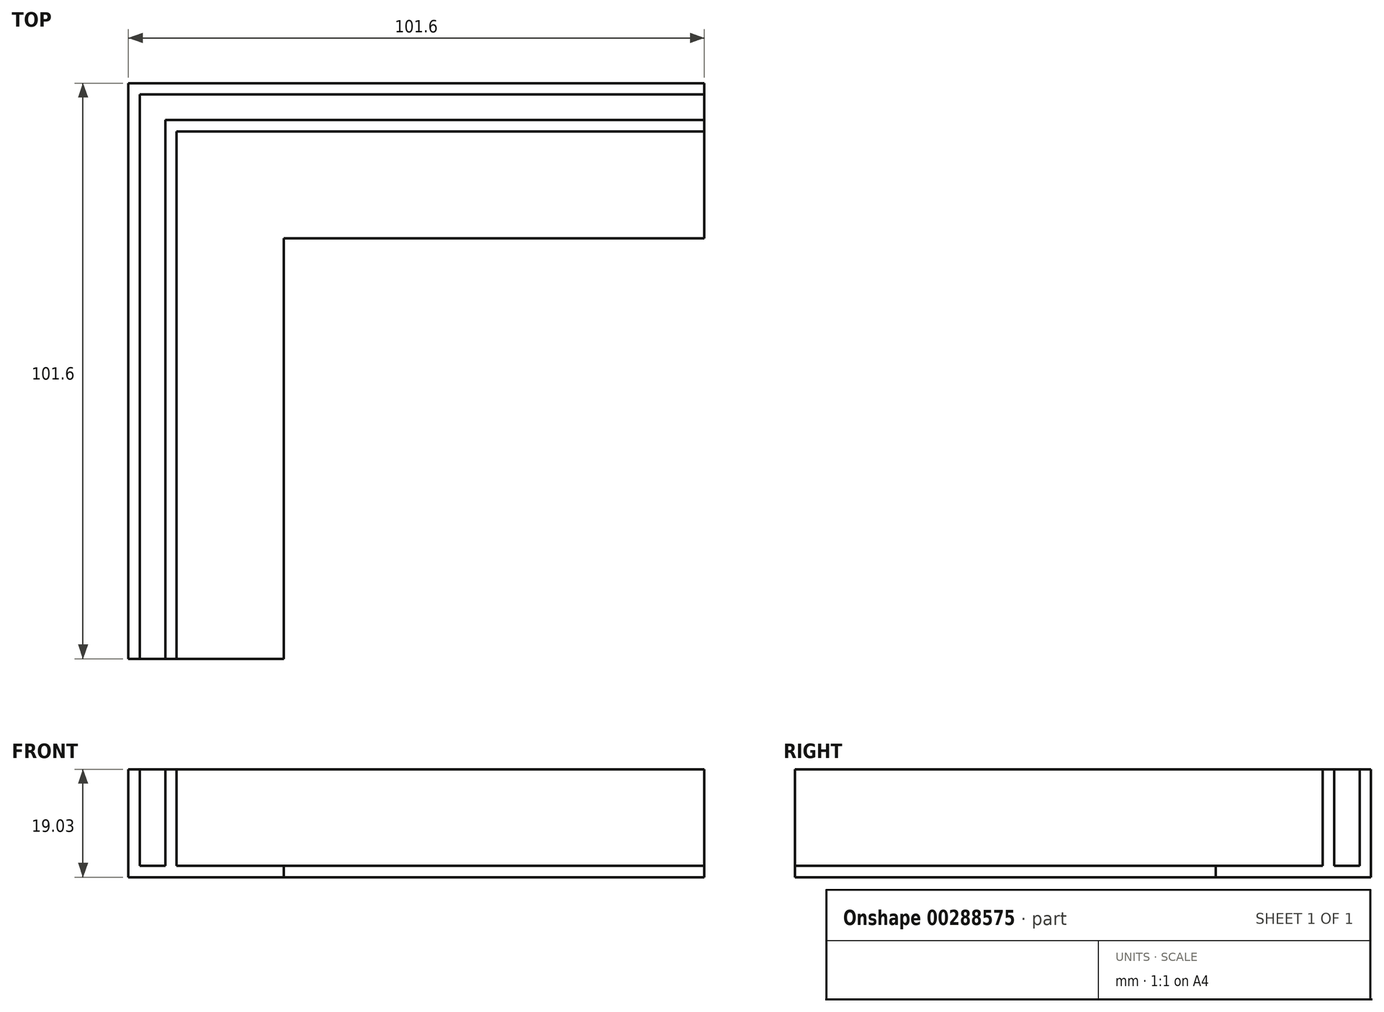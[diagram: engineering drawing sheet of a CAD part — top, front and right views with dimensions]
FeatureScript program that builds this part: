
annotation { "Feature Type Name" : "Feature", "Feature Type Description" : "" }
export const myFeature = defineFeature(function(context is Context, id is Id, definition is map)
    precondition{}
    {
        {
            var Q0;
            Q0=qCreatedBy(makeId("Top.planeOp"),FACE);
            var sketch = newSketch(context, id + "F0", { "sketchPlane" : qUnion([Q0])});
            skLineSegment(sketch, "E0.bottom", {"start": v(50.8, 50.8) * mm, "end": v(-50.8, 50.8) * mm});
            skLineSegment(sketch, "E0.top", {"start": v(50.8, -50.8) * mm, "end": v(-50.8, -50.8) * mm});
            skLineSegment(sketch, "E0.left", {"start": v(50.8, 50.8) * mm, "end": v(50.8, -50.8) * mm});
            skLineSegment(sketch, "E0.right", {"start": v(-50.8, 50.8) * mm, "end": v(-50.8, -50.8) * mm});
            skPoint(sketch, "E0.middle", {"position": v(0, 0) * mm});
            skSolve(sketch);
        }
        {
            var Q0;
            Q0 = qSketchRegion(id + "F0", true);
            extrude(context, id + "F1", {"entities" : qUnion([Q0]), "oppositeDirection" : true, "depth" : 2 * mm});
        }
        {
            var Q0;
            Q0=makeQuery(id+"F1.opExtrude","CAP_FACE",FACE,{"disambiguationData":[OSD([sQuery(id+"F0.wireOp",EDGE,"E0.bottom"),sQuery(id+"F0.wireOp",EDGE,"E0.top"),sQuery(id+"F0.wireOp",EDGE,"E0.left"),sQuery(id+"F0.wireOp",EDGE,"E0.right")])],"isStart":true});
            var sketch = newSketch(context, id + "F2", { "sketchPlane" : qUnion([Q0])});
            skLineSegment(sketch, "E1.right", {"start": v(-48.8, -50.8) * mm, "end": v(-48.8, 48.8) * mm});
            skLineSegment(sketch, "E2.top", {"start": v(50.8, 48.8) * mm, "end": v(-48.8, 48.8) * mm});
            skLineSegment(sketch, "E3", {"start": v(-50.8, 50.8) * mm, "end": v(-50.8, -50.8) * mm});
            skLineSegment(sketch, "E4", {"start": v(-50.8, -50.8) * mm, "end": v(-48.8, -50.8) * mm});
            skLineSegment(sketch, "E5", {"start": v(-50.8, 50.8) * mm, "end": v(50.8, 50.8) * mm});
            skLineSegment(sketch, "E6", {"start": v(50.8, 50.8) * mm, "end": v(50.8, 48.8) * mm});
            skSolve(sketch);
        }
        {
            var Q0;
            Q0=makeQuery(id+"F2.imprint","IMPRINT",FACE,{"disambiguationData":[TD([[makeQuery(id+"F2.imprint","IMPRINT",EDGE,{"derivedFrom":sQuery(id+"F2.wireOp",EDGE,"E1.right")}),1.0]])]});
            extrude(context, id + "F3", {"entities" : qUnion([Q0]), "operationType" : NewBodyOperationType.ADD, "depth" : 17.02 * mm});
        }
        {
            var Q0;
            Q0=makeQuery(id+"F1.opExtrude","CAP_FACE",FACE,{"disambiguationData":[OSD([sQuery(id+"F0.wireOp",EDGE,"E0.bottom"),sQuery(id+"F0.wireOp",EDGE,"E0.top"),sQuery(id+"F0.wireOp",EDGE,"E0.left"),sQuery(id+"F0.wireOp",EDGE,"E0.right")])],"isStart":true});
            var sketch = newSketch(context, id + "F4", { "sketchPlane" : qUnion([Q0])});
            skLineSegment(sketch, "E7.bottom", {"start": v(50.8, -50.8) * mm, "end": v(-44.3, -50.8) * mm});
            skLineSegment(sketch, "E7.top", {"start": v(50.8, 44.3) * mm, "end": v(-44.3, 44.3) * mm});
            skLineSegment(sketch, "E7.left", {"start": v(50.8, -50.8) * mm, "end": v(50.8, 44.3) * mm});
            skLineSegment(sketch, "E7.right", {"start": v(-44.3, -50.8) * mm, "end": v(-44.3, 44.3) * mm});
            skSolve(sketch);
        }
        {
            var Q0;
            Q0=makeQuery(id+"F4.imprint","IMPRINT",FACE,{"disambiguationData":[TD([[makeQuery(id+"F4.imprint","IMPRINT",EDGE,{"derivedFrom":sQuery(id+"F4.wireOp",EDGE,"E7.bottom")}),-1.0]])]});
            var Q1;
            Q1=makeQuery(id+"F3.opExtrude","CAP_FACE",FACE,{"disambiguationData":[OSD([sQuery(id+"F2.wireOp",EDGE,"E1.right"),sQuery(id+"F2.wireOp",EDGE,"E2.top"),sQuery(id+"F2.wireOp",EDGE,"E3"),sQuery(id+"F2.wireOp",EDGE,"E4"),sQuery(id+"F2.wireOp",EDGE,"E5"),sQuery(id+"F2.wireOp",EDGE,"E6")])],"isStart":false});
            extrude(context, id + "F5", {"entities" : qUnion([Q0]), "operationType" : NewBodyOperationType.ADD, "endBound" : BoundingType.UP_TO_SURFACE, "endBoundEntityFace" : qUnion([Q1]), "depth" : 25.4 * mm});
        }
        {
            var Q0;
            Q0=makeQuery(id+"F5.opExtrude","CAP_FACE",FACE,{"disambiguationData":[OSD([sQuery(id+"F4.wireOp",EDGE,"E7.bottom"),sQuery(id+"F4.wireOp",EDGE,"E7.top"),sQuery(id+"F4.wireOp",EDGE,"E7.left"),sQuery(id+"F4.wireOp",EDGE,"E7.right")])],"isStart":false});
            var sketch = newSketch(context, id + "F6", { "sketchPlane" : qUnion([Q0])});
            skLineSegment(sketch, "E8.bottom", {"start": v(50.8, -50.8) * mm, "end": v(-42.3, -50.8) * mm});
            skLineSegment(sketch, "E8.top", {"start": v(50.8, 42.3) * mm, "end": v(-42.3, 42.3) * mm});
            skLineSegment(sketch, "E8.left", {"start": v(50.8, -50.8) * mm, "end": v(50.8, 42.3) * mm});
            skLineSegment(sketch, "E8.right", {"start": v(-42.3, -50.8) * mm, "end": v(-42.3, 42.3) * mm});
            skSolve(sketch);
        }
        {
            var Q0;
            Q0=makeQuery(id+"F6.imprint","IMPRINT",FACE,{"disambiguationData":[TD([[makeQuery(id+"F6.imprint","IMPRINT",EDGE,{"derivedFrom":sQuery(id+"F6.wireOp",EDGE,"E8.bottom")}),-1.0]])]});
            extrude(context, id + "F7", {"entities" : qUnion([Q0]), "operationType" : NewBodyOperationType.REMOVE, "endBound" : BoundingType.THROUGH_ALL, "oppositeDirection" : true, "depth" : 59.5 * mm});
        }
        {
            var Q0;
            Q0=makeQuery(id+"F7.boolean.opBoolean","COPY",FACE,{"derivedFrom":makeQuery(id+"F7.opExtrude","SWEPT_FACE",FACE,{"disambiguationData":[OSD([sQuery(id+"F6.wireOp",EDGE,"E8.right")])]})});
            var sketch = newSketch(context, id + "F8", { "sketchPlane" : qUnion([Q0])});
            skLineSegment(sketch, "E9.bottom", {"start": v(-50.8, -2) * mm, "end": v(42.3, -2) * mm});
            skLineSegment(sketch, "E9.top", {"start": v(-50.8, 0) * mm, "end": v(42.3, 0) * mm});
            skLineSegment(sketch, "E9.left", {"start": v(-50.8, -2) * mm, "end": v(-50.8, 0) * mm});
            skLineSegment(sketch, "E9.right", {"start": v(42.3, -2) * mm, "end": v(42.3, 0) * mm});
            skSolve(sketch);
        }
        {
            var Q0;
            Q0=makeQuery(id+"F8.imprint","IMPRINT",FACE,{"disambiguationData":[TD([[makeQuery(id+"F8.imprint","IMPRINT",EDGE,{"derivedFrom":sQuery(id+"F8.wireOp",EDGE,"E9.bottom")}),1.0]])]});
            extrude(context, id + "F9", {"entities" : qUnion([Q0]), "operationType" : NewBodyOperationType.ADD, "depth" : 16.9 * mm + 2 * mm});
        }
        {
            var Q0;
            Q0=makeQuery(id+"F7.boolean.opBoolean","COPY",FACE,{"derivedFrom":makeQuery(id+"F7.opExtrude","SWEPT_FACE",FACE,{"disambiguationData":[OSD([sQuery(id+"F6.wireOp",EDGE,"E8.top")])]})});
            var sketch = newSketch(context, id + "F10", { "sketchPlane" : qUnion([Q0])});
            skLineSegment(sketch, "E10.bottom", {"start": v(50.8, -2) * mm, "end": v(-23.4, -2) * mm});
            skLineSegment(sketch, "E10.top", {"start": v(50.8, 0) * mm, "end": v(-23.4, 0) * mm});
            skLineSegment(sketch, "E10.left", {"start": v(50.8, -2) * mm, "end": v(50.8, 0) * mm});
            skLineSegment(sketch, "E10.right", {"start": v(-23.4, -2) * mm, "end": v(-23.4, 0) * mm});
            skSolve(sketch);
        }
        {
            var Q0;
            Q0=makeQuery(id+"F10.imprint","IMPRINT",FACE,{"disambiguationData":[TD([[makeQuery(id+"F10.imprint","IMPRINT",EDGE,{"derivedFrom":sQuery(id+"F10.wireOp",EDGE,"E10.bottom")}),-1.0]])]});
            extrude(context, id + "F11", {"entities" : qUnion([Q0]), "operationType" : NewBodyOperationType.ADD, "depth" : 18.9 * mm});
        }
    });
